# Revit family: CI122ZDTB5-US-CA
name_source: partatom
category: Specialty Equipment
units: mm (PartAtom-declared; Revit-internal decimal feet)

## family parameters
Always vertical = No
Cut with Voids When Loaded = Yes
Part Type = Normal
Room Calculation Point = No
Round Connector Dimension = Use Diameter
Shared = No
Work Plane-Based = Yes

## types (1)
- CI122ZDTB5
    Cavity - Depth = 490 mm  [stored 1.60761 ft]
    Cavity - Height = 650 mm  [stored 2.13255 ft]
    Cavity - Width = 265 mm  [stored 0.869423 ft]
    Clearance - Below Cooktop = 86 mm  [stored 0.282152 ft]
    Clearance - Overhead Rangehood = 650 mm  [stored 2.13255 ft]
    Default Elevation = 0 mm  [stored 0 ft]
    Description = 12inch Series 7 Induction Cooktop
    Manufacturer = Fisher & Paykel Appliances
    Model = CI122ZDTB5
    Product - Depth = 528 mm  [stored 1.73228 ft]
    Product - Height = 90 mm
    Product - Width = 298 mm  [stored 0.97769 ft]
    URL = www.fisherpaykel.com

note: [stored X ft] marks values corroborated as IEEE doubles in the binary element streams (Revit-internal decimal feet)

## geometry (parser evidence)
native form markers: Sweep x85
no freeform markers — native parametric forms only
